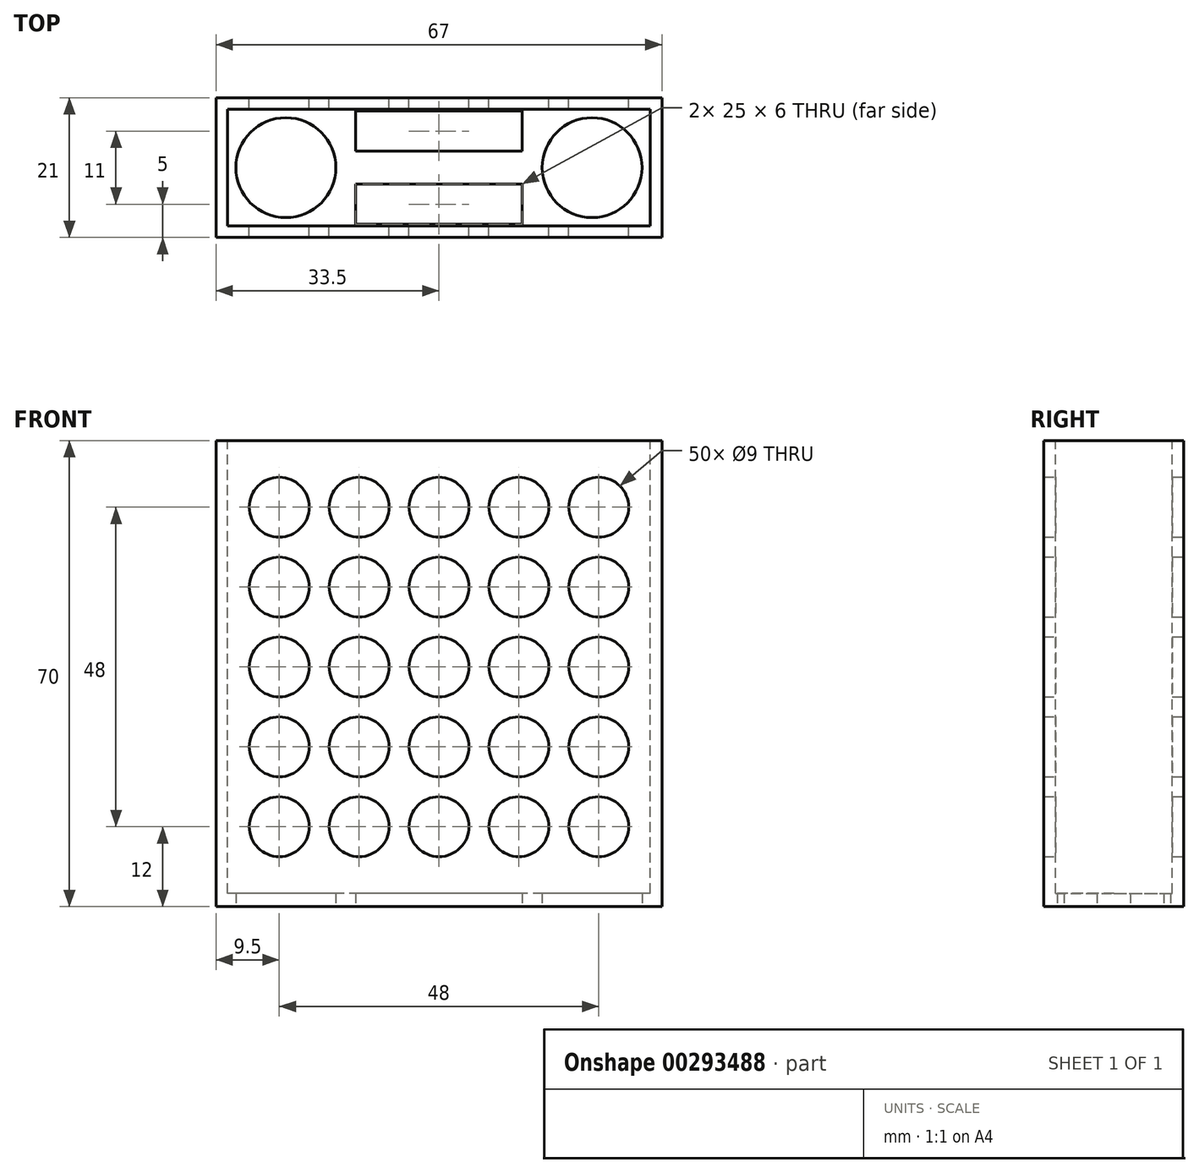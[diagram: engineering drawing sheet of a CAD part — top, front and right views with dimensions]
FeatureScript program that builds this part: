
annotation { "Feature Type Name" : "Feature", "Feature Type Description" : "" }
export const myFeature = defineFeature(function(context is Context, id is Id, definition is map)
    precondition{}
    {
        {
            var Q0;
            Q0=qCreatedBy(makeId("Top.planeOp"),FACE);
            var sketch = newSketch(context, id + "F0", { "sketchPlane" : qUnion([Q0])});
            skLineSegment(sketch, "E0.bottom", {"start": v(33.5, -10.5) * mm, "end": v(-33.5, -10.5) * mm});
            skLineSegment(sketch, "E0.top", {"start": v(33.5, 10.5) * mm, "end": v(-33.5, 10.5) * mm});
            skLineSegment(sketch, "E0.left", {"start": v(33.5, -10.5) * mm, "end": v(33.5, 10.5) * mm});
            skLineSegment(sketch, "E0.right", {"start": v(-33.5, -10.5) * mm, "end": v(-33.5, 10.5) * mm});
            skPoint(sketch, "E0.middle", {"position": v(0, 0) * mm});
            skSolve(sketch);
        }
        {
            var Q0;
            Q0 = qSketchRegion(id + "F0", true);
            extrude(context, id + "F1", {"entities" : qUnion([Q0]), "depth" : 70 * mm, "offsetDistance" : 25 * mm});
        }
        {
            var Q0;
            Q0=makeQuery(id+"F1.opExtrude","CAP_FACE",FACE,{"disambiguationData":[OSD([sQuery(id+"F0.wireOp",EDGE,"E0.bottom"),sQuery(id+"F0.wireOp",EDGE,"E0.top"),sQuery(id+"F0.wireOp",EDGE,"E0.left"),sQuery(id+"F0.wireOp",EDGE,"E0.right")])],"isStart":false});
            var sketch = newSketch(context, id + "F2", { "sketchPlane" : qUnion([Q0])});
            skLineSegment(sketch, "E1.bottom", {"start": v(31.75, -8.75) * mm, "end": v(-31.75, -8.75) * mm});
            skLineSegment(sketch, "E1.top", {"start": v(31.75, 8.75) * mm, "end": v(-31.75, 8.75) * mm});
            skLineSegment(sketch, "E1.left", {"start": v(31.75, -8.75) * mm, "end": v(31.75, 8.75) * mm});
            skLineSegment(sketch, "E1.right", {"start": v(-31.75, -8.75) * mm, "end": v(-31.75, 8.75) * mm});
            skPoint(sketch, "E1.middle", {"position": v(0, 0) * mm});
            skSolve(sketch);
        }
        {
            var Q0;
            Q0 = qSketchRegion(id + "F2", true);
            extrude(context, id + "F3", {"entities" : qUnion([Q0]), "operationType" : NewBodyOperationType.REMOVE, "oppositeDirection" : true, "depth" : 68 * mm, "offsetDistance" : 25 * mm});
        }
        {
            var Q0;
            Q0=makeQuery(id+"F1.opExtrude","CAP_FACE",FACE,{"disambiguationData":[OSD([sQuery(id+"F0.wireOp",EDGE,"E0.bottom"),sQuery(id+"F0.wireOp",EDGE,"E0.top"),sQuery(id+"F0.wireOp",EDGE,"E0.left"),sQuery(id+"F0.wireOp",EDGE,"E0.right")])],"isStart":true});
            var sketch = newSketch(context, id + "F4", { "sketchPlane" : qUnion([Q0])});
            skCircle(sketch, "E2", {"center": v(-23, 0) * mm, "radius": 7.5 * mm});
            skCircle(sketch, "E3.MirrorC", {"center": v(23, 0) * mm, "radius": 7.5 * mm});
            skLineSegment(sketch, "E4.bottom", {"start": v(12.5, 2.5) * mm, "end": v(-12.5, 2.5) * mm});
            skLineSegment(sketch, "E4.top", {"start": v(12.5, 8.5) * mm, "end": v(-12.5, 8.5) * mm});
            skLineSegment(sketch, "E4.left", {"start": v(12.5, 2.5) * mm, "end": v(12.5, 8.5) * mm});
            skLineSegment(sketch, "E4.right", {"start": v(-12.5, 2.5) * mm, "end": v(-12.5, 8.5) * mm});
            skLineSegment(sketch, "E5.MirrorCS", {"start": v(12.5, -2.5) * mm, "end": v(-12.5, -2.5) * mm});
            skLineSegment(sketch, "E6.MirrorCS", {"start": v(12.5, -8.5) * mm, "end": v(-12.5, -8.5) * mm});
            skLineSegment(sketch, "E7.MirrorCS", {"start": v(12.5, -2.5) * mm, "end": v(12.5, -8.5) * mm});
            skLineSegment(sketch, "E8.MirrorCS", {"start": v(-12.5, -2.5) * mm, "end": v(-12.5, -8.5) * mm});
            skSolve(sketch);
        }
        {
            var Q0;
            Q0 = qSketchRegion(id + "F4", true);
            extrude(context, id + "F5", {"entities" : qUnion([Q0]), "operationType" : NewBodyOperationType.REMOVE, "endBound" : BoundingType.UP_TO_NEXT, "oppositeDirection" : true, "depth" : 25 * mm, "offsetDistance" : 25 * mm});
        }
        {
            var Q0;
            Q0=makeQuery(id+"F1.opExtrude","SWEPT_FACE",FACE,{"disambiguationData":[OSD([sQuery(id+"F0.wireOp",EDGE,"E0.top")])]});
            var sketch = newSketch(context, id + "F6", { "sketchPlane" : qUnion([Q0])});
            skCircle(sketch, "E9", {"center": v(24, 60) * mm, "radius": 4.5 * mm});
            skCircle(sketch, "E10.0.1.0", {"center": v(24, 48) * mm, "radius": 4.5 * mm});
            skCircle(sketch, "E10.0.2.0", {"center": v(24, 36) * mm, "radius": 4.5 * mm});
            skCircle(sketch, "E10.0.3.0", {"center": v(24, 24) * mm, "radius": 4.5 * mm});
            skCircle(sketch, "E10.0.4.0", {"center": v(24, 12) * mm, "radius": 4.5 * mm});
            skCircle(sketch, "E10.1.0.0", {"center": v(12, 60) * mm, "radius": 4.5 * mm});
            skCircle(sketch, "E10.1.1.0", {"center": v(12, 48) * mm, "radius": 4.5 * mm});
            skCircle(sketch, "E10.1.2.0", {"center": v(12, 36) * mm, "radius": 4.5 * mm});
            skCircle(sketch, "E10.1.3.0", {"center": v(12, 24) * mm, "radius": 4.5 * mm});
            skCircle(sketch, "E10.1.4.0", {"center": v(12, 12) * mm, "radius": 4.5 * mm});
            skCircle(sketch, "E10.2.0.0", {"center": v(0, 60) * mm, "radius": 4.5 * mm});
            skCircle(sketch, "E10.2.1.0", {"center": v(0, 48) * mm, "radius": 4.5 * mm});
            skCircle(sketch, "E10.2.2.0", {"center": v(0, 36) * mm, "radius": 4.5 * mm});
            skCircle(sketch, "E10.2.3.0", {"center": v(0, 24) * mm, "radius": 4.5 * mm});
            skCircle(sketch, "E10.2.4.0", {"center": v(0, 12) * mm, "radius": 4.5 * mm});
            skCircle(sketch, "E10.3.0.0", {"center": v(-12, 60) * mm, "radius": 4.5 * mm});
            skCircle(sketch, "E10.3.1.0", {"center": v(-12, 48) * mm, "radius": 4.5 * mm});
            skCircle(sketch, "E10.3.2.0", {"center": v(-12, 36) * mm, "radius": 4.5 * mm});
            skCircle(sketch, "E10.3.3.0", {"center": v(-12, 24) * mm, "radius": 4.5 * mm});
            skCircle(sketch, "E10.3.4.0", {"center": v(-12, 12) * mm, "radius": 4.5 * mm});
            skCircle(sketch, "E10.4.0.0", {"center": v(-24, 60) * mm, "radius": 4.5 * mm});
            skCircle(sketch, "E10.4.1.0", {"center": v(-24, 48) * mm, "radius": 4.5 * mm});
            skCircle(sketch, "E10.4.2.0", {"center": v(-24, 36) * mm, "radius": 4.5 * mm});
            skCircle(sketch, "E10.4.3.0", {"center": v(-24, 24) * mm, "radius": 4.5 * mm});
            skCircle(sketch, "E10.4.4.0", {"center": v(-24, 12) * mm, "radius": 4.5 * mm});
            skLineSegment(sketch, "E10.direction1", {"start": v(24, 60) * mm, "end": v(12, 60) * mm, "construction": true});
            skLineSegment(sketch, "E10.direction2", {"start": v(24, 60) * mm, "end": v(24, 48) * mm, "construction": true});
            skSolve(sketch);
        }
        {
            var Q0;
            Q0 = qSketchRegion(id + "F6", true);
            extrude(context, id + "F7", {"entities" : qUnion([Q0]), "operationType" : NewBodyOperationType.REMOVE, "endBound" : BoundingType.THROUGH_ALL, "oppositeDirection" : true, "depth" : 25 * mm, "offsetDistance" : 25 * mm});
        }
    });
